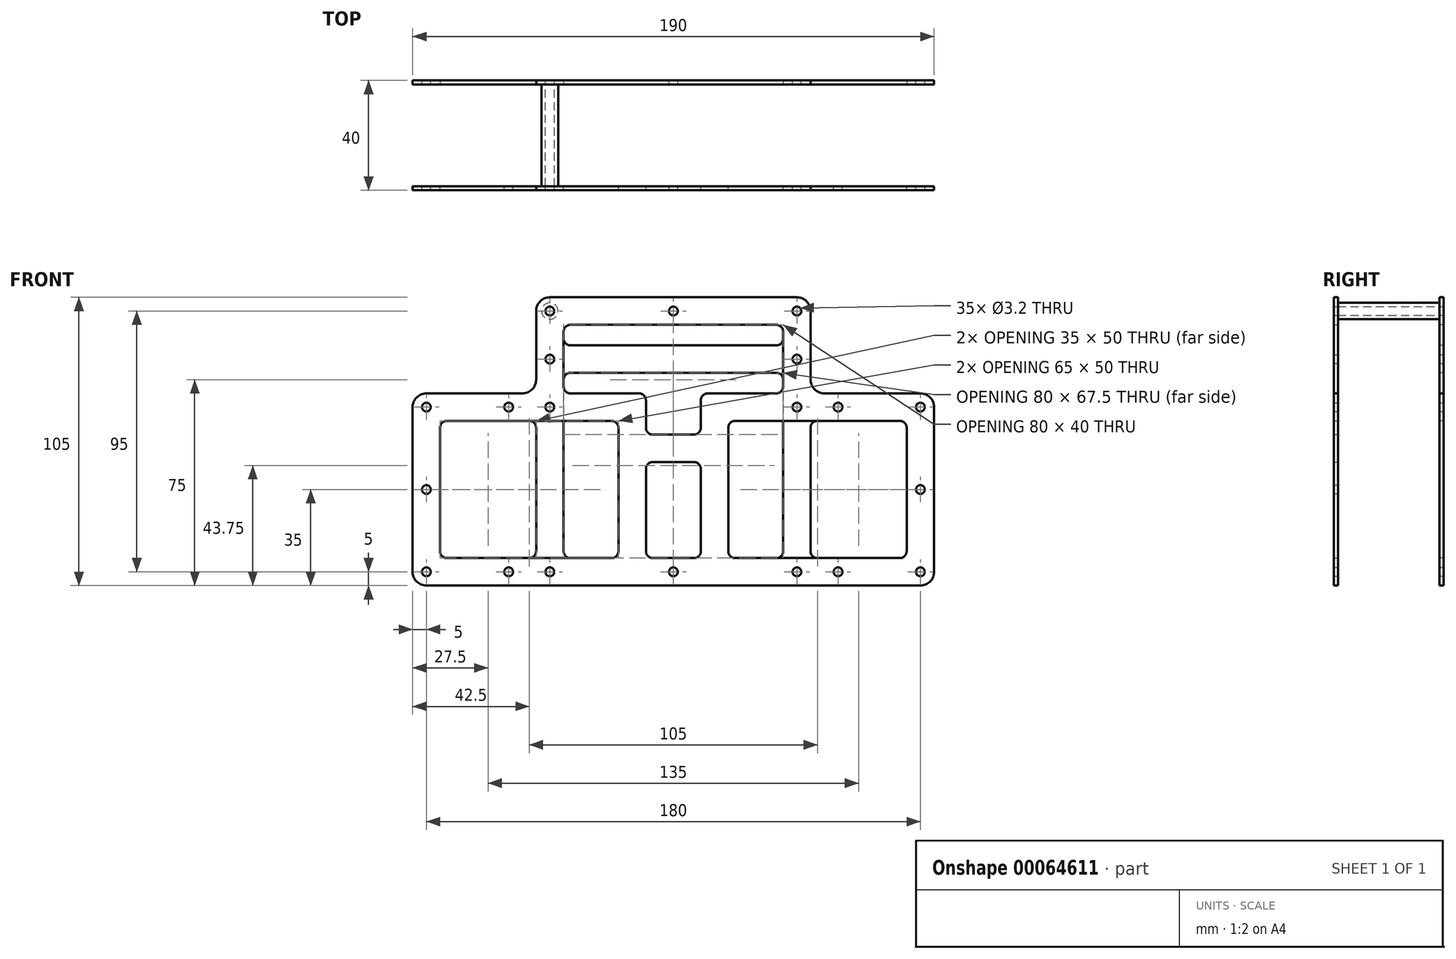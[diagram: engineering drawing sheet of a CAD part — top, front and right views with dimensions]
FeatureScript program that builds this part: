
annotation { "Feature Type Name" : "Feature", "Feature Type Description" : "" }
export const myFeature = defineFeature(function(context is Context, id is Id, definition is map)
    precondition{}
    {
        {
            assignVariable(context, id + "F0", {"name" : "middle", "anyValue" : 20 * mm});
        }
        {
            assignVariable(context, id + "F1", {"name" : "plate", "anyValue" : 1.5 * mm});
        }
        {
            var Q0;
            Q0=qCreatedBy(makeId("Front.planeOp"),FACE);
            var sketch = newSketch(context, id + "F2", { "sketchPlane" : qUnion([Q0])});
            skLineSegment(sketch, "E0.bottom", {"start": v(-90, 90) * mm, "end": v(-45, 90) * mm, "construction": true});
            skLineSegment(sketch, "E0.top", {"start": v(-90, -90) * mm, "end": v(90, -90) * mm, "construction": true});
            skLineSegment(sketch, "E0.left", {"start": v(-90, 90) * mm, "end": v(-90, 55) * mm, "construction": true});
            skLineSegment(sketch, "E0.right", {"start": v(90, 90) * mm, "end": v(90, 55) * mm, "construction": true});
            skLineSegment(sketch, "E1", {"start": v(0, 90) * mm, "end": v(0, -90) * mm, "construction": true});
            skLineSegment(sketch, "E2", {"start": v(-90, 55) * mm, "end": v(-15, 55) * mm, "construction": true});
            skLineSegment(sketch, "E3", {"start": v(90, -5) * mm, "end": v(15, -5) * mm, "construction": true});
            skLineSegment(sketch, "E4", {"start": v(-15, 55) * mm, "end": v(-15, 40) * mm, "construction": true});
            skLineSegment(sketch, "E5", {"start": v(15, -5) * mm, "end": v(15, 40) * mm, "construction": true});
            skLineSegment(sketch, "E6", {"start": v(65, -5) * mm, "end": v(65, -90) * mm, "construction": true});
            skLineSegment(sketch, "E7", {"start": v(-65, -5) * mm, "end": v(-65, -90) * mm, "construction": true});
            skLineSegment(sketch, "E8", {"start": v(-45, 90) * mm, "end": v(-45, 55) * mm, "construction": true});
            skLineSegment(sketch, "E9", {"start": v(45, 90) * mm, "end": v(45, 55) * mm, "construction": true});
            skLineSegment(sketch, "E10", {"start": v(15, 55) * mm, "end": v(90, 55) * mm, "construction": true});
            skLineSegment(sketch, "E11", {"start": v(-15, 40) * mm, "end": v(15, 40) * mm, "construction": true});
            skLineSegment(sketch, "E12", {"start": v(-15, -5) * mm, "end": v(-90, -5) * mm, "construction": true});
            skLineSegment(sketch, "E13", {"start": v(-90, -5) * mm, "end": v(-90, -90) * mm, "construction": true});
            skLineSegment(sketch, "E14", {"start": v(-90, 55) * mm, "end": v(-90, -5) * mm, "construction": true});
            skLineSegment(sketch, "E15", {"start": v(15, -5) * mm, "end": v(-15, -5) * mm, "construction": true});
            skLineSegment(sketch, "E16", {"start": v(90, -5) * mm, "end": v(90, -90) * mm, "construction": true});
            skLineSegment(sketch, "E17", {"start": v(90, 55) * mm, "end": v(90, -5) * mm, "construction": true});
            skLineSegment(sketch, "E18.0", {"start": v(-82.5, 50) * mm, "end": v(-22.5, 50) * mm});
            skLineSegment(sketch, "E18.1", {"start": v(-85, 47.5) * mm, "end": v(-85, 2.5) * mm});
            skLineSegment(sketch, "E18.2", {"start": v(-22.5, 0) * mm, "end": v(-82.5, 0) * mm});
            skLineSegment(sketch, "E18.3", {"start": v(-20, 47.5) * mm, "end": v(-20, 2.5) * mm});
            skLineSegment(sketch, "E19", {"start": v(-15, 40) * mm, "end": v(-15, -5) * mm, "construction": true});
            skLineSegment(sketch, "E20", {"start": v(15, 40) * mm, "end": v(15, 55) * mm, "construction": true});
            skLineSegment(sketch, "E21.0", {"start": v(-95, 55) * mm, "end": v(-95, -5) * mm});
            skLineSegment(sketch, "E21.2", {"start": v(-90, 60) * mm, "end": v(-55, 60) * mm});
            skLineSegment(sketch, "E21.4", {"start": v(90, -10) * mm, "end": v(-90, -10) * mm});
            skLineSegment(sketch, "E21.5", {"start": v(95, 55) * mm, "end": v(95, -5) * mm});
            skLineSegment(sketch, "E21.6", {"start": v(-10, 57.5) * mm, "end": v(-10, 47.5) * mm});
            skLineSegment(sketch, "E21.7", {"start": v(-7.5, 45) * mm, "end": v(7.5, 45) * mm});
            skLineSegment(sketch, "E21.8", {"start": v(10, 47.5) * mm, "end": v(10, 57.5) * mm});
            skLineSegment(sketch, "E21.9", {"start": v(12.5, 60) * mm, "end": v(37.5, 60) * mm});
            skLineSegment(sketch, "E22.0", {"start": v(-7.5, 35) * mm, "end": v(7.5, 35) * mm});
            skLineSegment(sketch, "E22.1", {"start": v(-10, 32.5) * mm, "end": v(-10, 2.5) * mm});
            skLineSegment(sketch, "E22.2", {"start": v(7.5, 0) * mm, "end": v(-7.5, 0) * mm});
            skLineSegment(sketch, "E22.3", {"start": v(10, 2.5) * mm, "end": v(10, 32.5) * mm});
            skLineSegment(sketch, "E23", {"start": v(-45, 90) * mm, "end": v(45, 90) * mm, "construction": true});
            skLineSegment(sketch, "E24", {"start": v(45, 90) * mm, "end": v(90, 90) * mm, "construction": true});
            skLineSegment(sketch, "E25.1", {"start": v(82.5, 0) * mm, "end": v(22.5, 0) * mm});
            skLineSegment(sketch, "E25.2", {"start": v(20, 2.5) * mm, "end": v(20, 47.5) * mm});
            skLineSegment(sketch, "E25.3", {"start": v(22.5, 50) * mm, "end": v(82.5, 50) * mm});
            skLineSegment(sketch, "E25.4", {"start": v(85, 47.5) * mm, "end": v(85, 2.5) * mm});
            skLineSegment(sketch, "E26.0", {"start": v(-50, 90) * mm, "end": v(-50, 65) * mm});
            skLineSegment(sketch, "E26.1", {"start": v(-45, 95) * mm, "end": v(45, 95) * mm});
            skLineSegment(sketch, "E26.2", {"start": v(50, 90) * mm, "end": v(50, 65) * mm});
            skLineSegment(sketch, "E27.0", {"start": v(-40, 82.5) * mm, "end": v(-40, 62.5) * mm});
            skLineSegment(sketch, "E27.1", {"start": v(-37.5, 85) * mm, "end": v(37.5, 85) * mm});
            skLineSegment(sketch, "E27.2", {"start": v(40, 82.5) * mm, "end": v(40, 62.5) * mm});
            skLineSegment(sketch, "E28", {"start": v(-37.5, 60) * mm, "end": v(-12.5, 60) * mm});
            skLineSegment(sketch, "E29", {"start": v(55, 60) * mm, "end": v(90, 60) * mm});
            skPoint(sketch, "E30.visualSharp", {"position": v(-40, 60) * mm});
            skArc(sketch, "E30.filletArc", {"start": v(-40, 62.5) * mm, "mid": v(-39.27, 60.73) * mm, "end": v(-37.5, 60) * mm});
            skPoint(sketch, "E31.visualSharp", {"position": v(40, 60) * mm});
            skArc(sketch, "E31.filletArc", {"start": v(37.5, 60) * mm, "mid": v(39.27, 60.73) * mm, "end": v(40, 62.5) * mm});
            skPoint(sketch, "E32.visualSharp", {"position": v(40, 85) * mm});
            skArc(sketch, "E32.filletArc", {"start": v(40, 82.5) * mm, "mid": v(39.27, 84.27) * mm, "end": v(37.5, 85) * mm});
            skPoint(sketch, "E33.visualSharp", {"position": v(-40, 85) * mm});
            skArc(sketch, "E33.filletArc", {"start": v(-37.5, 85) * mm, "mid": v(-39.27, 84.27) * mm, "end": v(-40, 82.5) * mm});
            skPoint(sketch, "E34.visualSharp", {"position": v(-10, 45) * mm});
            skArc(sketch, "E34.filletArc", {"start": v(-10, 47.5) * mm, "mid": v(-9.27, 45.73) * mm, "end": v(-7.5, 45) * mm});
            skPoint(sketch, "E35.visualSharp", {"position": v(-10, 60) * mm});
            skArc(sketch, "E35.filletArc", {"start": v(-10, 57.5) * mm, "mid": v(-10.73, 59.27) * mm, "end": v(-12.5, 60) * mm});
            skPoint(sketch, "E36.visualSharp", {"position": v(10, 60) * mm});
            skArc(sketch, "E36.filletArc", {"start": v(12.5, 60) * mm, "mid": v(10.73, 59.27) * mm, "end": v(10, 57.5) * mm});
            skPoint(sketch, "E37.visualSharp", {"position": v(10, 45) * mm});
            skArc(sketch, "E37.filletArc", {"start": v(7.5, 45) * mm, "mid": v(9.27, 45.73) * mm, "end": v(10, 47.5) * mm});
            skPoint(sketch, "E38.visualSharp", {"position": v(50, 95) * mm});
            skArc(sketch, "E38.filletArc", {"start": v(50, 90) * mm, "mid": v(48.54, 93.54) * mm, "end": v(45, 95) * mm});
            skPoint(sketch, "E39.visualSharp", {"position": v(-50, 95) * mm});
            skArc(sketch, "E39.filletArc", {"start": v(-45, 95) * mm, "mid": v(-48.54, 93.54) * mm, "end": v(-50, 90) * mm});
            skPoint(sketch, "E40.visualSharp", {"position": v(-95, 60) * mm});
            skArc(sketch, "E40.filletArc", {"start": v(-90, 60) * mm, "mid": v(-93.54, 58.54) * mm, "end": v(-95, 55) * mm});
            skPoint(sketch, "E41.visualSharp", {"position": v(-95, -10) * mm});
            skArc(sketch, "E41.filletArc", {"start": v(-95, -5) * mm, "mid": v(-93.54, -8.54) * mm, "end": v(-90, -10) * mm});
            skPoint(sketch, "E42.visualSharp", {"position": v(95, -10) * mm});
            skArc(sketch, "E42.filletArc", {"start": v(90, -10) * mm, "mid": v(93.54, -8.54) * mm, "end": v(95, -5) * mm});
            skPoint(sketch, "E43.visualSharp", {"position": v(95, 60) * mm});
            skArc(sketch, "E43.filletArc", {"start": v(95, 55) * mm, "mid": v(93.54, 58.54) * mm, "end": v(90, 60) * mm});
            skPoint(sketch, "E44.visualSharp", {"position": v(50, 60) * mm});
            skArc(sketch, "E44.filletArc", {"start": v(50, 65) * mm, "mid": v(51.46, 61.46) * mm, "end": v(55, 60) * mm});
            skPoint(sketch, "E45.visualSharp", {"position": v(-50, 60) * mm});
            skArc(sketch, "E45.filletArc", {"start": v(-55, 60) * mm, "mid": v(-51.46, 61.46) * mm, "end": v(-50, 65) * mm});
            skPoint(sketch, "E46.visualSharp", {"position": v(-10, 35) * mm});
            skArc(sketch, "E46.filletArc", {"start": v(-7.5, 35) * mm, "mid": v(-9.27, 34.27) * mm, "end": v(-10, 32.5) * mm});
            skPoint(sketch, "E47.visualSharp", {"position": v(-10, 0) * mm});
            skArc(sketch, "E47.filletArc", {"start": v(-10, 2.5) * mm, "mid": v(-9.27, 0.73) * mm, "end": v(-7.5, 0) * mm});
            skPoint(sketch, "E48.visualSharp", {"position": v(10, 0) * mm});
            skArc(sketch, "E48.filletArc", {"start": v(7.5, 0) * mm, "mid": v(9.27, 0.73) * mm, "end": v(10, 2.5) * mm});
            skPoint(sketch, "E49.visualSharp", {"position": v(10, 35) * mm});
            skArc(sketch, "E49.filletArc", {"start": v(10, 32.5) * mm, "mid": v(9.27, 34.27) * mm, "end": v(7.5, 35) * mm});
            skPoint(sketch, "E50.visualSharp", {"position": v(20, 50) * mm});
            skArc(sketch, "E50.filletArc", {"start": v(22.5, 50) * mm, "mid": v(20.73, 49.27) * mm, "end": v(20, 47.5) * mm});
            skPoint(sketch, "E51.visualSharp", {"position": v(20, 0) * mm});
            skArc(sketch, "E51.filletArc", {"start": v(20, 2.5) * mm, "mid": v(20.73, 0.73) * mm, "end": v(22.5, 0) * mm});
            skPoint(sketch, "E52.visualSharp", {"position": v(85, 0) * mm});
            skArc(sketch, "E52.filletArc", {"start": v(82.5, 0) * mm, "mid": v(84.27, 0.73) * mm, "end": v(85, 2.5) * mm});
            skPoint(sketch, "E53.visualSharp", {"position": v(85, 50) * mm});
            skArc(sketch, "E53.filletArc", {"start": v(85, 47.5) * mm, "mid": v(84.27, 49.27) * mm, "end": v(82.5, 50) * mm});
            skPoint(sketch, "E54.visualSharp", {"position": v(-20, 50) * mm});
            skArc(sketch, "E54.filletArc", {"start": v(-20, 47.5) * mm, "mid": v(-20.73, 49.27) * mm, "end": v(-22.5, 50) * mm});
            skPoint(sketch, "E55.visualSharp", {"position": v(-20, 0) * mm});
            skArc(sketch, "E55.filletArc", {"start": v(-22.5, 0) * mm, "mid": v(-20.73, 0.73) * mm, "end": v(-20, 2.5) * mm});
            skPoint(sketch, "E56.visualSharp", {"position": v(-85, 0) * mm});
            skArc(sketch, "E56.filletArc", {"start": v(-85, 2.5) * mm, "mid": v(-84.27, 0.73) * mm, "end": v(-82.5, 0) * mm});
            skPoint(sketch, "E57.visualSharp", {"position": v(-85, 50) * mm});
            skArc(sketch, "E57.filletArc", {"start": v(-82.5, 50) * mm, "mid": v(-84.27, 49.27) * mm, "end": v(-85, 47.5) * mm});
            skCircle(sketch, "E58", {"center": v(60, 25) * mm, "radius": 30 * mm, "construction": true});
            skCircle(sketch, "E59", {"center": v(60, 55) * mm, "radius": 1.6 * mm});
            skCircle(sketch, "E60", {"center": v(90, 25) * mm, "radius": 1.6 * mm});
            skCircle(sketch, "E61", {"center": v(60, -5) * mm, "radius": 1.6 * mm});
            skCircle(sketch, "E62.MirrorC", {"center": v(-60, 55) * mm, "radius": 1.6 * mm});
            skCircle(sketch, "E63.MirrorC", {"center": v(-90, 25) * mm, "radius": 1.6 * mm});
            skCircle(sketch, "E64.MirrorC", {"center": v(-60, -5) * mm, "radius": 1.6 * mm});
            skSolve(sketch);
        }
        {
            var Q0;
            Q0=makeQuery(id+"F2.imprint","IMPRINT",FACE,{"disambiguationData":[TD([[makeQuery(id+"F2.imprint","IMPRINT",EDGE,{"derivedFrom":sQuery(id+"F2.wireOp",EDGE,"E18.0")}),1.0]])]});
            extrude(context, id + "F3", {"entities" : qUnion([Q0]), "depth" : getVariable(context, 'middle'), "hasSecondDirection" : true, "secondDirectionOppositeDirection" : false, "secondDirectionDepth" : getVariable(context, 'middle') - getVariable(context, 'plate')});
        }
        {
            var Q0;
            Q0=qCreatedBy(makeId("Front.planeOp"),FACE);
            var sketch = newSketch(context, id + "F4", { "sketchPlane" : qUnion([Q0])});
            skLineSegment(sketch, "E65.0", {"start": v(-50, 90) * mm, "end": v(-50, 65) * mm});
            skArc(sketch, "E65.1", {"start": v(-55, 60) * mm, "mid": v(-51.46, 61.46) * mm, "end": v(-50, 65) * mm});
            skLineSegment(sketch, "E65.2", {"start": v(-90, 60) * mm, "end": v(-55, 60) * mm});
            skArc(sketch, "E65.3", {"start": v(-90, 60) * mm, "mid": v(-93.54, 58.54) * mm, "end": v(-95, 55) * mm});
            skLineSegment(sketch, "E65.4", {"start": v(-95, 55) * mm, "end": v(-95, -5) * mm});
            skArc(sketch, "E65.5", {"start": v(-95, -5) * mm, "mid": v(-93.54, -8.54) * mm, "end": v(-90, -10) * mm});
            skLineSegment(sketch, "E65.6", {"start": v(90, -10) * mm, "end": v(-90, -10) * mm});
            skArc(sketch, "E65.7", {"start": v(90, -10) * mm, "mid": v(93.54, -8.54) * mm, "end": v(95, -5) * mm});
            skLineSegment(sketch, "E65.8", {"start": v(95, 55) * mm, "end": v(95, -5) * mm});
            skArc(sketch, "E65.9", {"start": v(95, 55) * mm, "mid": v(93.54, 58.54) * mm, "end": v(90, 60) * mm});
            skLineSegment(sketch, "E65.10", {"start": v(55, 60) * mm, "end": v(90, 60) * mm});
            skArc(sketch, "E65.11", {"start": v(50, 65) * mm, "mid": v(51.46, 61.46) * mm, "end": v(55, 60) * mm});
            skLineSegment(sketch, "E65.12", {"start": v(50, 90) * mm, "end": v(50, 65) * mm});
            skArc(sketch, "E65.13", {"start": v(50, 90) * mm, "mid": v(48.54, 93.54) * mm, "end": v(45, 95) * mm});
            skLineSegment(sketch, "E65.14", {"start": v(-45, 95) * mm, "end": v(45, 95) * mm});
            skArc(sketch, "E65.15", {"start": v(-45, 95) * mm, "mid": v(-48.54, 93.54) * mm, "end": v(-50, 90) * mm});
            skLineSegment(sketch, "E66", {"start": v(-45, 90) * mm, "end": v(-45, 72.5) * mm, "construction": true});
            skLineSegment(sketch, "E67", {"start": v(45, 90) * mm, "end": v(45, 72.5) * mm, "construction": true});
            skLineSegment(sketch, "E68.0", {"start": v(90, 55) * mm, "end": v(90, -5) * mm, "construction": true});
            skLineSegment(sketch, "E68.1", {"start": v(-90, 55) * mm, "end": v(-90, -5) * mm, "construction": true});
            skLineSegment(sketch, "E69", {"start": v(-45, 55) * mm, "end": v(-45, -5) * mm, "construction": true});
            skLineSegment(sketch, "E70", {"start": v(45, 55) * mm, "end": v(45, -5) * mm, "construction": true});
            skLineSegment(sketch, "E71", {"start": v(-45, 72.5) * mm, "end": v(-45, 55) * mm, "construction": true});
            skLineSegment(sketch, "E72", {"start": v(45, 72.5) * mm, "end": v(45, 55) * mm, "construction": true});
            skLineSegment(sketch, "E73", {"start": v(-45, 72.5) * mm, "end": v(45, 72.5) * mm, "construction": true});
            skLineSegment(sketch, "E74", {"start": v(-45, 55) * mm, "end": v(-90, 55) * mm, "construction": true});
            skLineSegment(sketch, "E75", {"start": v(-90, -5) * mm, "end": v(-45, -5) * mm, "construction": true});
            skLineSegment(sketch, "E76", {"start": v(45, -5) * mm, "end": v(-45, -5) * mm, "construction": true});
            skLineSegment(sketch, "E77", {"start": v(45, -5) * mm, "end": v(90, -5) * mm, "construction": true});
            skLineSegment(sketch, "E78", {"start": v(90, 55) * mm, "end": v(45, 55) * mm, "construction": true});
            skLineSegment(sketch, "E79", {"start": v(-45, 90) * mm, "end": v(45, 90) * mm, "construction": true});
            skLineSegment(sketch, "E80.0", {"start": v(-85, 47.5) * mm, "end": v(-85, 2.5) * mm});
            skLineSegment(sketch, "E80.1", {"start": v(-52.5, 50) * mm, "end": v(-82.5, 50) * mm});
            skLineSegment(sketch, "E80.2", {"start": v(-50, 47.5) * mm, "end": v(-50, 2.5) * mm});
            skLineSegment(sketch, "E80.3", {"start": v(-82.5, 0) * mm, "end": v(-52.5, 0) * mm});
            skLineSegment(sketch, "E81.0", {"start": v(85, 47.5) * mm, "end": v(85, 2.5) * mm});
            skLineSegment(sketch, "E81.1", {"start": v(82.5, 50) * mm, "end": v(52.5, 50) * mm});
            skLineSegment(sketch, "E81.2", {"start": v(50, 47.5) * mm, "end": v(50, 2.5) * mm});
            skLineSegment(sketch, "E81.3", {"start": v(52.5, 0) * mm, "end": v(82.5, 0) * mm});
            skLineSegment(sketch, "E82.2", {"start": v(40, 65) * mm, "end": v(40, 2.5) * mm});
            skLineSegment(sketch, "E82.3", {"start": v(-37.5, 67.5) * mm, "end": v(37.5, 67.5) * mm});
            skLineSegment(sketch, "E82.4", {"start": v(37.5, 0) * mm, "end": v(-37.5, 0) * mm});
            skLineSegment(sketch, "E82.5", {"start": v(-40, 65) * mm, "end": v(-40, 2.5) * mm});
            skLineSegment(sketch, "E83.0", {"start": v(-37.5, 85) * mm, "end": v(37.5, 85) * mm});
            skLineSegment(sketch, "E83.1", {"start": v(-40, 82.5) * mm, "end": v(-40, 80) * mm});
            skLineSegment(sketch, "E83.2", {"start": v(-37.5, 77.5) * mm, "end": v(37.5, 77.5) * mm});
            skLineSegment(sketch, "E83.3", {"start": v(40, 82.5) * mm, "end": v(40, 80) * mm});
            skPoint(sketch, "E84.visualSharp", {"position": v(-40, 67.5) * mm});
            skArc(sketch, "E84.filletArc", {"start": v(-37.5, 67.5) * mm, "mid": v(-39.27, 66.77) * mm, "end": v(-40, 65) * mm});
            skPoint(sketch, "E85.visualSharp", {"position": v(40, 67.5) * mm});
            skArc(sketch, "E85.filletArc", {"start": v(40, 65) * mm, "mid": v(39.27, 66.77) * mm, "end": v(37.5, 67.5) * mm});
            skPoint(sketch, "E86.visualSharp", {"position": v(40, 0) * mm});
            skArc(sketch, "E86.filletArc", {"start": v(37.5, 0) * mm, "mid": v(39.27, 0.73) * mm, "end": v(40, 2.5) * mm});
            skPoint(sketch, "E87.visualSharp", {"position": v(-40, 0) * mm});
            skArc(sketch, "E87.filletArc", {"start": v(-40, 2.5) * mm, "mid": v(-39.27, 0.73) * mm, "end": v(-37.5, 0) * mm});
            skPoint(sketch, "E88.visualSharp", {"position": v(-50, 0) * mm});
            skArc(sketch, "E88.filletArc", {"start": v(-52.5, 0) * mm, "mid": v(-50.73, 0.73) * mm, "end": v(-50, 2.5) * mm});
            skPoint(sketch, "E89.visualSharp", {"position": v(-50, 50) * mm});
            skArc(sketch, "E89.filletArc", {"start": v(-50, 47.5) * mm, "mid": v(-50.73, 49.27) * mm, "end": v(-52.5, 50) * mm});
            skPoint(sketch, "E90.visualSharp", {"position": v(-85, 50) * mm});
            skArc(sketch, "E90.filletArc", {"start": v(-82.5, 50) * mm, "mid": v(-84.27, 49.27) * mm, "end": v(-85, 47.5) * mm});
            skPoint(sketch, "E91.visualSharp", {"position": v(-85, 0) * mm});
            skArc(sketch, "E91.filletArc", {"start": v(-85, 2.5) * mm, "mid": v(-84.27, 0.73) * mm, "end": v(-82.5, 0) * mm});
            skPoint(sketch, "E92.visualSharp", {"position": v(50, 0) * mm});
            skArc(sketch, "E92.filletArc", {"start": v(50, 2.5) * mm, "mid": v(50.73, 0.73) * mm, "end": v(52.5, 0) * mm});
            skPoint(sketch, "E93.visualSharp", {"position": v(50, 50) * mm});
            skArc(sketch, "E93.filletArc", {"start": v(52.5, 50) * mm, "mid": v(50.73, 49.27) * mm, "end": v(50, 47.5) * mm});
            skPoint(sketch, "E94.visualSharp", {"position": v(85, 0) * mm});
            skArc(sketch, "E94.filletArc", {"start": v(82.5, 0) * mm, "mid": v(84.27, 0.73) * mm, "end": v(85, 2.5) * mm});
            skPoint(sketch, "E95.visualSharp", {"position": v(85, 50) * mm});
            skArc(sketch, "E95.filletArc", {"start": v(85, 47.5) * mm, "mid": v(84.27, 49.27) * mm, "end": v(82.5, 50) * mm});
            skPoint(sketch, "E96.visualSharp", {"position": v(40, 85) * mm});
            skArc(sketch, "E96.filletArc", {"start": v(40, 82.5) * mm, "mid": v(39.27, 84.27) * mm, "end": v(37.5, 85) * mm});
            skPoint(sketch, "E97.visualSharp", {"position": v(-40, 85) * mm});
            skArc(sketch, "E97.filletArc", {"start": v(-37.5, 85) * mm, "mid": v(-39.27, 84.27) * mm, "end": v(-40, 82.5) * mm});
            skPoint(sketch, "E98.visualSharp", {"position": v(-40, 77.5) * mm});
            skArc(sketch, "E98.filletArc", {"start": v(-40, 80) * mm, "mid": v(-39.27, 78.23) * mm, "end": v(-37.5, 77.5) * mm});
            skPoint(sketch, "E99.visualSharp", {"position": v(40, 77.5) * mm});
            skArc(sketch, "E99.filletArc", {"start": v(37.5, 77.5) * mm, "mid": v(39.27, 78.23) * mm, "end": v(40, 80) * mm});
            skCircle(sketch, "E100", {"center": v(-90, 55) * mm, "radius": 3 * mm});
            skCircle(sketch, "E101", {"center": v(-45, 55) * mm, "radius": 3 * mm});
            skCircle(sketch, "E102", {"center": v(-45, -5) * mm, "radius": 3 * mm});
            skCircle(sketch, "E103", {"center": v(-90, -5) * mm, "radius": 3 * mm});
            skCircle(sketch, "E104", {"center": v(90, -5) * mm, "radius": 3 * mm});
            skCircle(sketch, "E105", {"center": v(45, -5) * mm, "radius": 3 * mm});
            skCircle(sketch, "E106", {"center": v(45, 55) * mm, "radius": 3 * mm});
            skCircle(sketch, "E107", {"center": v(90, 55) * mm, "radius": 3 * mm});
            skCircle(sketch, "E108", {"center": v(45, 72.5) * mm, "radius": 3 * mm});
            skCircle(sketch, "E109", {"center": v(45, 90) * mm, "radius": 3 * mm});
            skCircle(sketch, "E110", {"center": v(-45, 72.5) * mm, "radius": 3 * mm});
            skCircle(sketch, "E111", {"center": v(-45, 90) * mm, "radius": 3 * mm});
            skCircle(sketch, "E112", {"center": v(0, -5) * mm, "radius": 3 * mm});
            skCircle(sketch, "E113", {"center": v(0, 90) * mm, "radius": 3 * mm});
            skCircle(sketch, "E114", {"center": v(-90, 55) * mm, "radius": 1.6 * mm});
            skCircle(sketch, "E115", {"center": v(-45, 55) * mm, "radius": 1.6 * mm});
            skCircle(sketch, "E116", {"center": v(-45, 72.5) * mm, "radius": 1.6 * mm});
            skCircle(sketch, "E117", {"center": v(-45, 90) * mm, "radius": 1.6 * mm});
            skCircle(sketch, "E118", {"center": v(0, 90) * mm, "radius": 1.6 * mm});
            skCircle(sketch, "E119", {"center": v(-90, -5) * mm, "radius": 1.6 * mm});
            skCircle(sketch, "E120", {"center": v(-45, -5) * mm, "radius": 1.6 * mm});
            skCircle(sketch, "E121", {"center": v(0, -5) * mm, "radius": 1.6 * mm});
            skCircle(sketch, "E122", {"center": v(45, -5) * mm, "radius": 1.6 * mm});
            skCircle(sketch, "E123", {"center": v(90, -5) * mm, "radius": 1.6 * mm});
            skCircle(sketch, "E124", {"center": v(90, 55) * mm, "radius": 1.6 * mm});
            skCircle(sketch, "E125", {"center": v(45, 55) * mm, "radius": 1.6 * mm});
            skCircle(sketch, "E126", {"center": v(45, 90) * mm, "radius": 1.6 * mm});
            skCircle(sketch, "E127", {"center": v(45, 72.5) * mm, "radius": 1.6 * mm});
            skSolve(sketch);
        }
        {
            var Q0;
            Q0=makeQuery(id+"F4.imprint","IMPRINT",FACE,{"disambiguationData":[TD([[makeQuery(id+"F4.imprint","IMPRINT",EDGE,{"derivedFrom":sQuery(id+"F4.wireOp",EDGE,"E65.0")}),1.0]])]});
            var Q1;
            Q1=makeQuery(id+"F4.imprint","IMPRINT",FACE,{"disambiguationData":[TD([[makeQuery(id+"F4.imprint","IMPRINT",EDGE,{"derivedFrom":sQuery(id+"F4.wireOp",EDGE,"E120")}),1.0]])]});
            var Q2;
            Q2=makeQuery(id+"F4.imprint","IMPRINT",FACE,{"disambiguationData":[TD([[makeQuery(id+"F4.imprint","IMPRINT",EDGE,{"derivedFrom":sQuery(id+"F4.wireOp",EDGE,"E102")}),1.0]])]});
            var Q3;
            Q3=makeQuery(id+"F4.imprint","IMPRINT",FACE,{"disambiguationData":[TD([[makeQuery(id+"F4.imprint","IMPRINT",EDGE,{"derivedFrom":sQuery(id+"F4.wireOp",EDGE,"E103")}),1.0]])]});
            var Q4;
            Q4=makeQuery(id+"F4.imprint","IMPRINT",FACE,{"disambiguationData":[TD([[makeQuery(id+"F4.imprint","IMPRINT",EDGE,{"derivedFrom":sQuery(id+"F4.wireOp",EDGE,"E104")}),1.0]])]});
            var Q5;
            Q5=makeQuery(id+"F4.imprint","IMPRINT",FACE,{"disambiguationData":[TD([[makeQuery(id+"F4.imprint","IMPRINT",EDGE,{"derivedFrom":sQuery(id+"F4.wireOp",EDGE,"E105")}),1.0]])]});
            var Q6;
            Q6=makeQuery(id+"F4.imprint","IMPRINT",FACE,{"disambiguationData":[TD([[makeQuery(id+"F4.imprint","IMPRINT",EDGE,{"derivedFrom":sQuery(id+"F4.wireOp",EDGE,"E112")}),1.0]])]});
            var Q7;
            Q7=makeQuery(id+"F4.imprint","IMPRINT",FACE,{"disambiguationData":[TD([[makeQuery(id+"F4.imprint","IMPRINT",EDGE,{"derivedFrom":sQuery(id+"F4.wireOp",EDGE,"E123")}),1.0]])]});
            var Q8;
            Q8=makeQuery(id+"F4.imprint","IMPRINT",FACE,{"disambiguationData":[TD([[makeQuery(id+"F4.imprint","IMPRINT",EDGE,{"derivedFrom":sQuery(id+"F4.wireOp",EDGE,"E119")}),1.0]])]});
            var Q9;
            Q9=makeQuery(id+"F4.imprint","IMPRINT",FACE,{"disambiguationData":[TD([[makeQuery(id+"F4.imprint","IMPRINT",EDGE,{"derivedFrom":sQuery(id+"F4.wireOp",EDGE,"E121")}),1.0]])]});
            var Q10;
            Q10=makeQuery(id+"F4.imprint","IMPRINT",FACE,{"disambiguationData":[TD([[makeQuery(id+"F4.imprint","IMPRINT",EDGE,{"derivedFrom":sQuery(id+"F4.wireOp",EDGE,"E122")}),1.0]])]});
            var Q11;
            Q11=makeQuery(id+"F4.imprint","IMPRINT",FACE,{"disambiguationData":[TD([[makeQuery(id+"F4.imprint","IMPRINT",EDGE,{"derivedFrom":sQuery(id+"F4.wireOp",EDGE,"E113")}),1.0]])]});
            var Q12;
            Q12=makeQuery(id+"F4.imprint","IMPRINT",FACE,{"disambiguationData":[TD([[makeQuery(id+"F4.imprint","IMPRINT",EDGE,{"derivedFrom":sQuery(id+"F4.wireOp",EDGE,"E111")}),1.0]])]});
            var Q13;
            Q13=makeQuery(id+"F4.imprint","IMPRINT",FACE,{"disambiguationData":[TD([[makeQuery(id+"F4.imprint","IMPRINT",EDGE,{"derivedFrom":sQuery(id+"F4.wireOp",EDGE,"E109")}),1.0]])]});
            var Q14;
            Q14=makeQuery(id+"F4.imprint","IMPRINT",FACE,{"disambiguationData":[TD([[makeQuery(id+"F4.imprint","IMPRINT",EDGE,{"derivedFrom":sQuery(id+"F4.wireOp",EDGE,"E126")}),1.0]])]});
            var Q15;
            Q15=makeQuery(id+"F4.imprint","IMPRINT",FACE,{"disambiguationData":[TD([[makeQuery(id+"F4.imprint","IMPRINT",EDGE,{"derivedFrom":sQuery(id+"F4.wireOp",EDGE,"E118")}),1.0]])]});
            var Q16;
            Q16=makeQuery(id+"F4.imprint","IMPRINT",FACE,{"disambiguationData":[TD([[makeQuery(id+"F4.imprint","IMPRINT",EDGE,{"derivedFrom":sQuery(id+"F4.wireOp",EDGE,"E117")}),1.0]])]});
            var Q17;
            Q17=makeQuery(id+"F4.imprint","IMPRINT",FACE,{"disambiguationData":[TD([[makeQuery(id+"F4.imprint","IMPRINT",EDGE,{"derivedFrom":sQuery(id+"F4.wireOp",EDGE,"E110")}),1.0]])]});
            var Q18;
            Q18=makeQuery(id+"F4.imprint","IMPRINT",FACE,{"disambiguationData":[TD([[makeQuery(id+"F4.imprint","IMPRINT",EDGE,{"derivedFrom":sQuery(id+"F4.wireOp",EDGE,"E100")}),1.0]])]});
            var Q19;
            Q19=makeQuery(id+"F4.imprint","IMPRINT",FACE,{"disambiguationData":[TD([[makeQuery(id+"F4.imprint","IMPRINT",EDGE,{"derivedFrom":sQuery(id+"F4.wireOp",EDGE,"E115")}),1.0]])]});
            var Q20;
            Q20=makeQuery(id+"F4.imprint","IMPRINT",FACE,{"disambiguationData":[TD([[makeQuery(id+"F4.imprint","IMPRINT",EDGE,{"derivedFrom":sQuery(id+"F4.wireOp",EDGE,"E101")}),1.0]])]});
            var Q21;
            Q21=makeQuery(id+"F4.imprint","IMPRINT",FACE,{"disambiguationData":[TD([[makeQuery(id+"F4.imprint","IMPRINT",EDGE,{"derivedFrom":sQuery(id+"F4.wireOp",EDGE,"E114")}),1.0]])]});
            var Q22;
            Q22=makeQuery(id+"F4.imprint","IMPRINT",FACE,{"disambiguationData":[TD([[makeQuery(id+"F4.imprint","IMPRINT",EDGE,{"derivedFrom":sQuery(id+"F4.wireOp",EDGE,"E116")}),1.0]])]});
            var Q23;
            Q23=makeQuery(id+"F4.imprint","IMPRINT",FACE,{"disambiguationData":[TD([[makeQuery(id+"F4.imprint","IMPRINT",EDGE,{"derivedFrom":sQuery(id+"F4.wireOp",EDGE,"E106")}),1.0]])]});
            var Q24;
            Q24=makeQuery(id+"F4.imprint","IMPRINT",FACE,{"disambiguationData":[TD([[makeQuery(id+"F4.imprint","IMPRINT",EDGE,{"derivedFrom":sQuery(id+"F4.wireOp",EDGE,"E107")}),1.0]])]});
            var Q25;
            Q25=makeQuery(id+"F4.imprint","IMPRINT",FACE,{"disambiguationData":[TD([[makeQuery(id+"F4.imprint","IMPRINT",EDGE,{"derivedFrom":sQuery(id+"F4.wireOp",EDGE,"E108")}),1.0]])]});
            var Q26;
            Q26=makeQuery(id+"F4.imprint","IMPRINT",FACE,{"disambiguationData":[TD([[makeQuery(id+"F4.imprint","IMPRINT",EDGE,{"derivedFrom":sQuery(id+"F4.wireOp",EDGE,"E127")}),1.0]])]});
            var Q27;
            Q27=makeQuery(id+"F4.imprint","IMPRINT",FACE,{"disambiguationData":[TD([[makeQuery(id+"F4.imprint","IMPRINT",EDGE,{"derivedFrom":sQuery(id+"F4.wireOp",EDGE,"E125")}),1.0]])]});
            var Q28;
            Q28=makeQuery(id+"F4.imprint","IMPRINT",FACE,{"disambiguationData":[TD([[makeQuery(id+"F4.imprint","IMPRINT",EDGE,{"derivedFrom":sQuery(id+"F4.wireOp",EDGE,"E124")}),1.0]])]});
            extrude(context, id + "F5", {"entities" : qUnion([Q0, Q1, Q2, Q3, Q4, Q5, Q6, Q7, Q8, Q9, Q10, Q11, Q12, Q13, Q14, Q15, Q16, Q17, Q18, Q19, Q20, Q21, Q22, Q23, Q24, Q25, Q26, Q27, Q28]), "oppositeDirection" : true, "depth" : getVariable(context, 'middle'), "hasSecondDirection" : true, "secondDirectionOppositeDirection" : true, "secondDirectionDepth" : getVariable(context, 'middle') - getVariable(context, 'plate')});
        }
        {
            var Q0;
            Q0=makeQuery(id+"F4.imprint","IMPRINT",FACE,{"disambiguationData":[TD([[makeQuery(id+"F4.imprint","IMPRINT",EDGE,{"derivedFrom":sQuery(id+"F4.wireOp",EDGE,"E111")}),1.0]])]});
            var Q1;
            Q1=sQuery(id+"F4.wireOp",EDGE,"E100");
            extrude(context, id + "F6", {"entities" : qUnion([Q0]), "surfaceEntities" : qUnion([Q1]), "endBound" : BoundingType.UP_TO_NEXT, "depth" : 25 * mm, "hasSecondDirection" : true, "secondDirectionBound" : SecondDirectionBoundingType.UP_TO_NEXT, "secondDirectionOppositeDirection" : true, "secondDirectionDepth" : 25 * mm});
        }
        {
            var Q0;
            Q0=makeQuery(id+"F4.imprint","IMPRINT",FACE,{"disambiguationData":[TD([[makeQuery(id+"F4.imprint","IMPRINT",EDGE,{"derivedFrom":sQuery(id+"F4.wireOp",EDGE,"E119")}),1.0]])]});
            var Q1;
            Q1=makeQuery(id+"F4.imprint","IMPRINT",FACE,{"disambiguationData":[TD([[makeQuery(id+"F4.imprint","IMPRINT",EDGE,{"derivedFrom":sQuery(id+"F4.wireOp",EDGE,"E120")}),1.0]])]});
            var Q2;
            Q2=makeQuery(id+"F4.imprint","IMPRINT",FACE,{"disambiguationData":[TD([[makeQuery(id+"F4.imprint","IMPRINT",EDGE,{"derivedFrom":sQuery(id+"F4.wireOp",EDGE,"E121")}),1.0]])]});
            var Q3;
            Q3=makeQuery(id+"F4.imprint","IMPRINT",FACE,{"disambiguationData":[TD([[makeQuery(id+"F4.imprint","IMPRINT",EDGE,{"derivedFrom":sQuery(id+"F4.wireOp",EDGE,"E122")}),1.0]])]});
            var Q4;
            Q4=makeQuery(id+"F4.imprint","IMPRINT",FACE,{"disambiguationData":[TD([[makeQuery(id+"F4.imprint","IMPRINT",EDGE,{"derivedFrom":sQuery(id+"F4.wireOp",EDGE,"E123")}),1.0]])]});
            var Q5;
            Q5=makeQuery(id+"F4.imprint","IMPRINT",FACE,{"disambiguationData":[TD([[makeQuery(id+"F4.imprint","IMPRINT",EDGE,{"derivedFrom":sQuery(id+"F4.wireOp",EDGE,"E125")}),1.0]])]});
            var Q6;
            Q6=makeQuery(id+"F4.imprint","IMPRINT",FACE,{"disambiguationData":[TD([[makeQuery(id+"F4.imprint","IMPRINT",EDGE,{"derivedFrom":sQuery(id+"F4.wireOp",EDGE,"E124")}),1.0]])]});
            var Q7;
            Q7=makeQuery(id+"F4.imprint","IMPRINT",FACE,{"disambiguationData":[TD([[makeQuery(id+"F4.imprint","IMPRINT",EDGE,{"derivedFrom":sQuery(id+"F4.wireOp",EDGE,"E127")}),1.0]])]});
            var Q8;
            Q8=makeQuery(id+"F4.imprint","IMPRINT",FACE,{"disambiguationData":[TD([[makeQuery(id+"F4.imprint","IMPRINT",EDGE,{"derivedFrom":sQuery(id+"F4.wireOp",EDGE,"E126")}),1.0]])]});
            var Q9;
            Q9=makeQuery(id+"F4.imprint","IMPRINT",FACE,{"disambiguationData":[TD([[makeQuery(id+"F4.imprint","IMPRINT",EDGE,{"derivedFrom":sQuery(id+"F4.wireOp",EDGE,"E118")}),1.0]])]});
            var Q10;
            Q10=makeQuery(id+"F4.imprint","IMPRINT",FACE,{"disambiguationData":[TD([[makeQuery(id+"F4.imprint","IMPRINT",EDGE,{"derivedFrom":sQuery(id+"F4.wireOp",EDGE,"E117")}),1.0]])]});
            var Q11;
            Q11=makeQuery(id+"F4.imprint","IMPRINT",FACE,{"disambiguationData":[TD([[makeQuery(id+"F4.imprint","IMPRINT",EDGE,{"derivedFrom":sQuery(id+"F4.wireOp",EDGE,"E116")}),1.0]])]});
            var Q12;
            Q12=makeQuery(id+"F4.imprint","IMPRINT",FACE,{"disambiguationData":[TD([[makeQuery(id+"F4.imprint","IMPRINT",EDGE,{"derivedFrom":sQuery(id+"F4.wireOp",EDGE,"E115")}),1.0]])]});
            var Q13;
            Q13=makeQuery(id+"F4.imprint","IMPRINT",FACE,{"disambiguationData":[TD([[makeQuery(id+"F4.imprint","IMPRINT",EDGE,{"derivedFrom":sQuery(id+"F4.wireOp",EDGE,"E114")}),1.0]])]});
            extrude(context, id + "F7", {"entities" : qUnion([Q0, Q1, Q2, Q3, Q4, Q5, Q6, Q7, Q8, Q9, Q10, Q11, Q12, Q13]), "operationType" : NewBodyOperationType.REMOVE, "endBound" : BoundingType.THROUGH_ALL, "depth" : 25 * mm, "hasSecondDirection" : true, "secondDirectionBound" : SecondDirectionBoundingType.THROUGH_ALL, "secondDirectionOppositeDirection" : true, "secondDirectionDepth" : 25 * mm});
        }
    });
